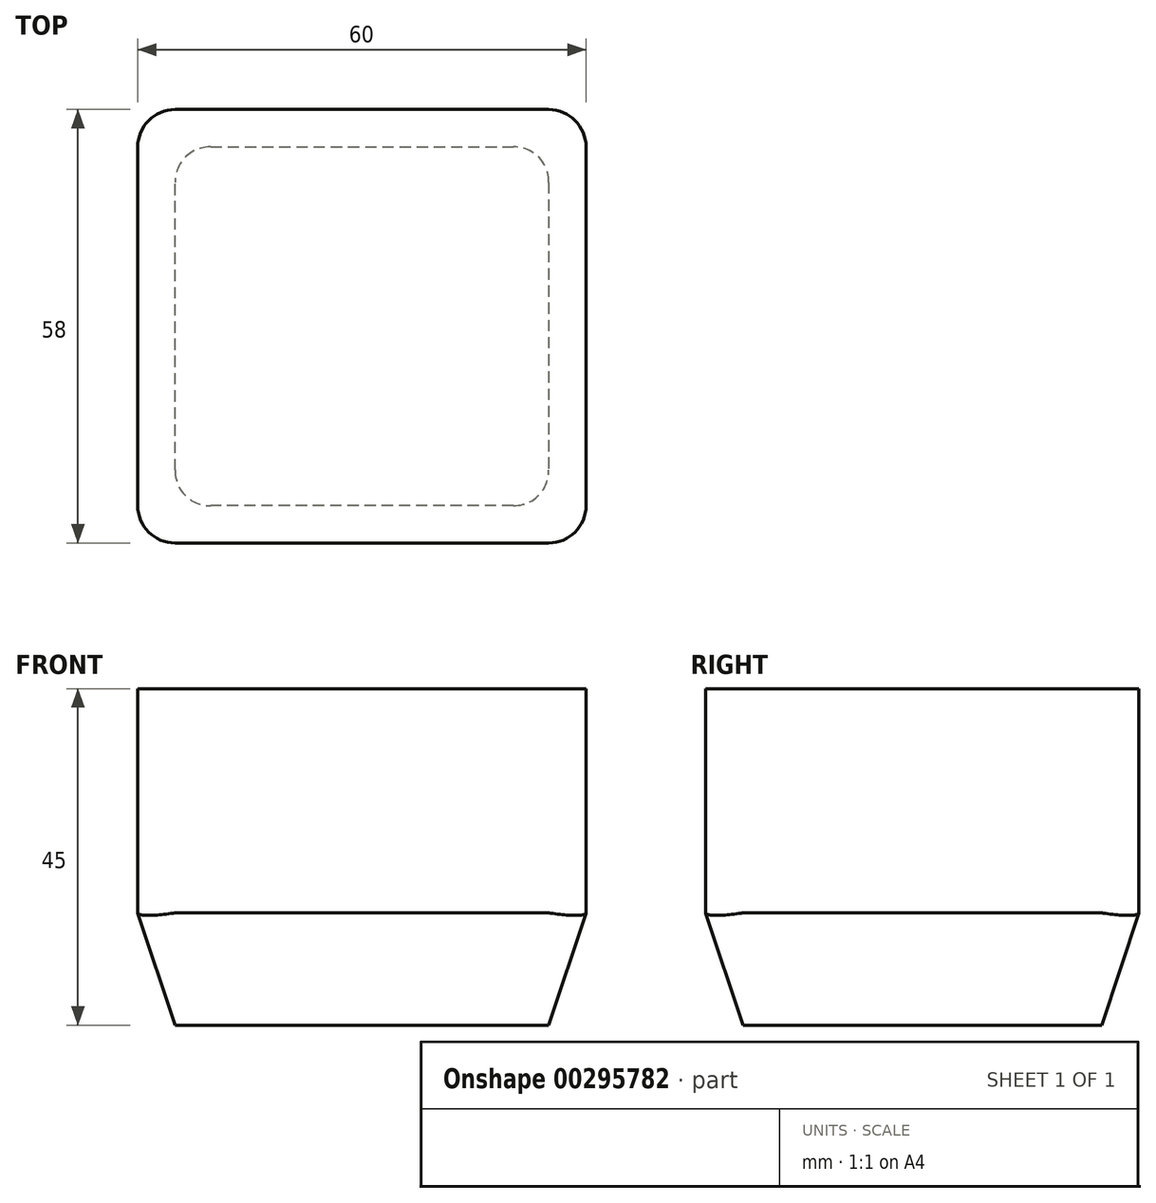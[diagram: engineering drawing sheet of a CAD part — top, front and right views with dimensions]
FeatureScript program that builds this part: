
annotation { "Feature Type Name" : "Feature", "Feature Type Description" : "" }
export const myFeature = defineFeature(function(context is Context, id is Id, definition is map)
    precondition{}
    {
        {
            var Q0;
            Q0=qCreatedBy(makeId("Top.planeOp"),FACE);
            var sketch = newSketch(context, id + "F0", { "sketchPlane" : qUnion([Q0])});
            skLineSegment(sketch, "E0.bottom", {"start": v(30, 29) * mm, "end": v(-30, 29) * mm});
            skLineSegment(sketch, "E0.top", {"start": v(30, -29) * mm, "end": v(-30, -29) * mm});
            skLineSegment(sketch, "E0.left", {"start": v(30, 29) * mm, "end": v(30, -29) * mm});
            skLineSegment(sketch, "E0.right", {"start": v(-30, 29) * mm, "end": v(-30, -29) * mm});
            skPoint(sketch, "E0.middle", {"position": v(0, 0) * mm});
            skSolve(sketch);
        }
        {
            var Q0;
            Q0=makeQuery(id+"F0.imprint","IMPRINT",FACE,{"disambiguationData":[TD([[makeQuery(id+"F0.imprint","IMPRINT",EDGE,{"derivedFrom":sQuery(id+"F0.wireOp",EDGE,"E0.bottom")}),1.0]])]});
            extrude(context, id + "F1", {"entities" : qUnion([Q0]), "depth" : 45 * mm, "offsetDistance" : 25 * mm});
        }
        {
            var Q0;
            Q0=makeQuery(id+"F1.opExtrude","CAP_FACE",FACE,{"disambiguationData":[OSD([sQuery(id+"F0.wireOp",EDGE,"E0.bottom"),sQuery(id+"F0.wireOp",EDGE,"E0.top"),sQuery(id+"F0.wireOp",EDGE,"E0.left"),sQuery(id+"F0.wireOp",EDGE,"E0.right")])],"isStart":true});
            chamfer(context, id + "F2", {"entities" : qUnion([Q0]), "chamferType" : ChamferType.TWO_OFFSETS, "width1" : 5 * mm, "oppositeDirection" : true, "width2" : 15 * mm, "tangentPropagation" : true});
        }
        {
            var Q0;
            Q0=makeQuery(id+"F1.opExtrude","SWEPT_EDGE",EDGE,{"disambiguationData":[OSD([sQuery(id+"F0.wireOp",EDGE,"E0.top"),sQuery(id+"F0.wireOp",EDGE,"E0.right")])]});
            var Q1;
            Q1=makeQuery(id+"F1.opExtrude","SWEPT_EDGE",EDGE,{"disambiguationData":[OSD([sQuery(id+"F0.wireOp",EDGE,"E0.top"),sQuery(id+"F0.wireOp",EDGE,"E0.left")])]});
            var Q2;
            Q2=makeQuery(id+"F1.opExtrude","SWEPT_EDGE",EDGE,{"disambiguationData":[OSD([sQuery(id+"F0.wireOp",EDGE,"E0.bottom"),sQuery(id+"F0.wireOp",EDGE,"E0.left")])]});
            var Q3;
            Q3=makeQuery(id+"F1.opExtrude","SWEPT_EDGE",EDGE,{"disambiguationData":[OSD([sQuery(id+"F0.wireOp",EDGE,"E0.bottom"),sQuery(id+"F0.wireOp",EDGE,"E0.right")])]});
            var Q4;
            Q4=makeQuery(id+"F2.opChamfer","BLEND_EDGE",EDGE,{"blendedFrom":[makeQuery(id+"F1.opExtrude","CAP_EDGE",EDGE,{"disambiguationData":[OSD([sQuery(id+"F0.wireOp",EDGE,"E0.top")])],"isStart":true}),makeQuery(id+"F1.opExtrude","CAP_EDGE",EDGE,{"disambiguationData":[OSD([sQuery(id+"F0.wireOp",EDGE,"E0.left")])],"isStart":true})],"blendedInto":[]});
            var Q5;
            Q5=makeQuery(id+"F2.opChamfer","BLEND_EDGE",EDGE,{"blendedFrom":[makeQuery(id+"F1.opExtrude","CAP_EDGE",EDGE,{"disambiguationData":[OSD([sQuery(id+"F0.wireOp",EDGE,"E0.bottom")])],"isStart":true}),makeQuery(id+"F1.opExtrude","CAP_EDGE",EDGE,{"disambiguationData":[OSD([sQuery(id+"F0.wireOp",EDGE,"E0.left")])],"isStart":true})],"blendedInto":[]});
            var Q6;
            Q6=makeQuery(id+"F2.opChamfer","BLEND_EDGE",EDGE,{"blendedFrom":[makeQuery(id+"F1.opExtrude","CAP_EDGE",EDGE,{"disambiguationData":[OSD([sQuery(id+"F0.wireOp",EDGE,"E0.bottom")])],"isStart":true}),makeQuery(id+"F1.opExtrude","CAP_EDGE",EDGE,{"disambiguationData":[OSD([sQuery(id+"F0.wireOp",EDGE,"E0.right")])],"isStart":true})],"blendedInto":[]});
            var Q7;
            Q7=makeQuery(id+"F2.opChamfer","BLEND_EDGE",EDGE,{"blendedFrom":[makeQuery(id+"F1.opExtrude","CAP_EDGE",EDGE,{"disambiguationData":[OSD([sQuery(id+"F0.wireOp",EDGE,"E0.top")])],"isStart":true}),makeQuery(id+"F1.opExtrude","CAP_EDGE",EDGE,{"disambiguationData":[OSD([sQuery(id+"F0.wireOp",EDGE,"E0.right")])],"isStart":true})],"blendedInto":[]});
            fillet(context, id + "F3", {"entities" : qUnion([Q0, Q1, Q2, Q3, Q4, Q5, Q6, Q7]), "radius" : 5 * mm, "tangentPropagation" : true, "allowEdgeOverflow" : false});
        }
    });
